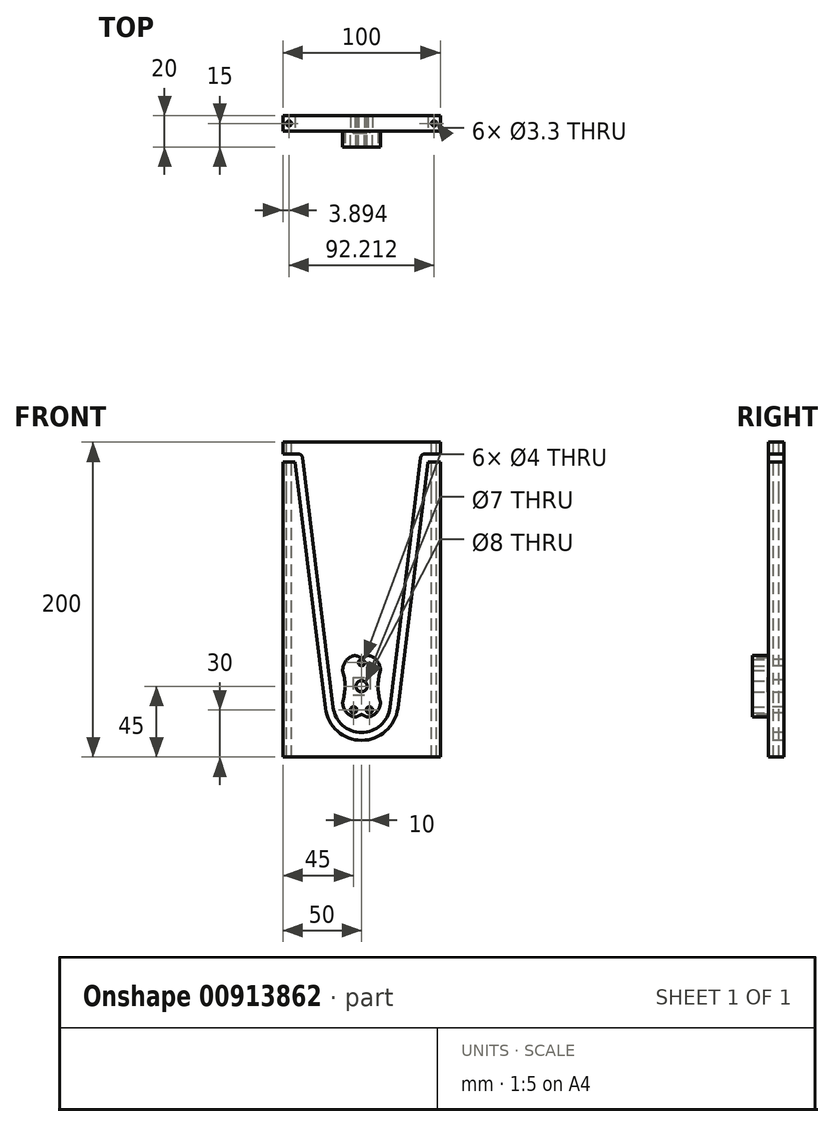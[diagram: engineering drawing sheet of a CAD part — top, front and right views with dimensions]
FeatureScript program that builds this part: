
annotation { "Feature Type Name" : "Feature", "Feature Type Description" : "" }
export const myFeature = defineFeature(function(context is Context, id is Id, definition is map)
    precondition{}
    {
        {
            var Q0;
            Q0=qCreatedBy(makeId("Front.planeOp"),FACE);
            var sketch = newSketch(context, id + "F0", { "sketchPlane" : qUnion([Q0])});
            skLineSegment(sketch, "E0.bottom", {"start": v(0, 0) * mm, "end": v(100, 0) * mm});
            skLineSegment(sketch, "E0.top", {"start": v(0, -200) * mm, "end": v(100, -200) * mm});
            skLineSegment(sketch, "E0.left", {"start": v(0, 0) * mm, "end": v(0, -200) * mm});
            skLineSegment(sketch, "E0.right", {"start": v(100, 0) * mm, "end": v(100, -200) * mm});
            skSolve(sketch);
        }
        {
            var Q0;
            Q0=makeQuery(id+"F0.imprint","IMPRINT",FACE,{"disambiguationData":[TD([[makeQuery(id+"F0.imprint","IMPRINT",EDGE,{"derivedFrom":sQuery(id+"F0.wireOp",EDGE,"E0.bottom")}),-1.0]])]});
            extrude(context, id + "F1", {"entities" : qUnion([Q0]), "depth" : 10 * mm, "offsetDistance" : 25 * mm});
        }
        {
            var Q0;
            Q0=makeQuery(id+"F1.opExtrude","CAP_FACE",FACE,{"disambiguationData":[OSD([sQuery(id+"F0.wireOp",EDGE,"E0.bottom"),sQuery(id+"F0.wireOp",EDGE,"E0.top"),sQuery(id+"F0.wireOp",EDGE,"E0.left"),sQuery(id+"F0.wireOp",EDGE,"E0.right")])],"isStart":false});
            var sketch = newSketch(context, id + "F2", { "sketchPlane" : qUnion([Q0])});
            skLineSegment(sketch, "E1", {"start": v(50, 0) * mm, "end": v(50, -200) * mm, "construction": true});
            skCircle(sketch, "E2", {"center": v(50, -155) * mm, "radius": 4 * mm});
            skCircle(sketch, "E3", {"center": v(55, -170) * mm, "radius": 2 * mm});
            skCircle(sketch, "E4", {"center": v(45, -170) * mm, "radius": 2 * mm});
            skCircle(sketch, "E5", {"center": v(50, -140) * mm, "radius": 2 * mm});
            skSolve(sketch);
        }
        {
            var Q0;
            Q0=qSketchRegion(id+"F2",true);
            extrude(context, id + "F3", {"entities" : qUnion([Q0]), "operationType" : NewBodyOperationType.REMOVE, "endBound" : BoundingType.THROUGH_ALL, "oppositeDirection" : true, "depth" : 25 * mm, "offsetDistance" : 25 * mm});
        }
        {
            var Q0;
            Q0=makeQuery(id+"F1.opExtrude","CAP_FACE",FACE,{"disambiguationData":[OSD([sQuery(id+"F0.wireOp",EDGE,"E0.bottom"),sQuery(id+"F0.wireOp",EDGE,"E0.top"),sQuery(id+"F0.wireOp",EDGE,"E0.left"),sQuery(id+"F0.wireOp",EDGE,"E0.right")])],"isStart":false});
            var sketch = newSketch(context, id + "F4", { "sketchPlane" : qUnion([Q0])});
            skLineSegment(sketch, "E6", {"start": v(50, 0) * mm, "end": v(50, -200) * mm, "construction": true});
            skLineSegment(sketch, "E7", {"start": v(0, -10) * mm, "end": v(10, -10) * mm});
            skLineSegment(sketch, "E8", {"start": v(10, -10) * mm, "end": v(29.48, -168.69) * mm});
            skArc(sketch, "E9", {"start": v(29.48, -168.69) * mm, "mid": v(36.3, -181.65) * mm, "end": v(50, -186.84) * mm});
            skLineSegment(sketch, "E10.MirrorCS", {"start": v(100, -10) * mm, "end": v(90, -10) * mm});
            skLineSegment(sketch, "E11.MirrorCS", {"start": v(90, -10) * mm, "end": v(70.52, -168.69) * mm});
            skArc(sketch, "E12.MirrorCS", {"start": v(70.52, -168.69) * mm, "mid": v(63.7, -181.65) * mm, "end": v(50, -186.84) * mm});
            skArc(sketch, "E13.0.startCap", {"start": v(87.52, -9.7) * mm, "mid": v(90.3, -7.52) * mm, "end": v(92.48, -10.3) * mm});
            skArc(sketch, "E13.0.endCap", {"start": v(73, -169) * mm, "mid": v(70.21, -171.17) * mm, "end": v(68.03, -168.38) * mm});
            skLineSegment(sketch, "E13.0.left", {"start": v(92.48, -10.3) * mm, "end": v(73, -169) * mm});
            skLineSegment(sketch, "E13.0.right", {"start": v(87.52, -9.7) * mm, "end": v(68.03, -168.38) * mm});
            skArc(sketch, "E13.1.startCap", {"start": v(100, -7.5) * mm, "mid": v(102.5, -10) * mm, "end": v(100, -12.5) * mm});
            skArc(sketch, "E13.1.endCap", {"start": v(90, -12.5) * mm, "mid": v(87.5, -10) * mm, "end": v(90, -7.5) * mm});
            skLineSegment(sketch, "E13.1.left", {"start": v(100, -12.5) * mm, "end": v(90, -12.5) * mm});
            skLineSegment(sketch, "E13.1.right", {"start": v(100, -7.5) * mm, "end": v(90, -7.5) * mm});
            skArc(sketch, "E13.2.startCap", {"start": v(0, -12.5) * mm, "mid": v(-2.5, -10) * mm, "end": v(0, -7.5) * mm});
            skArc(sketch, "E13.2.endCap", {"start": v(10, -7.5) * mm, "mid": v(12.5, -10) * mm, "end": v(10, -12.5) * mm});
            skLineSegment(sketch, "E13.2.left", {"start": v(0, -7.5) * mm, "end": v(10, -7.5) * mm});
            skLineSegment(sketch, "E13.2.right", {"start": v(0, -12.5) * mm, "end": v(10, -12.5) * mm});
            skArc(sketch, "E13.3.startCap", {"start": v(7.52, -10.3) * mm, "mid": v(9.7, -7.52) * mm, "end": v(12.48, -9.7) * mm});
            skArc(sketch, "E13.3.endCap", {"start": v(31.97, -168.38) * mm, "mid": v(29.79, -171.17) * mm, "end": v(27, -169) * mm});
            skLineSegment(sketch, "E13.3.left", {"start": v(12.48, -9.7) * mm, "end": v(31.97, -168.38) * mm});
            skLineSegment(sketch, "E13.3.right", {"start": v(7.52, -10.3) * mm, "end": v(27, -169) * mm});
            skArc(sketch, "E13.4.startCap", {"start": v(27, -169) * mm, "mid": v(29.18, -166.2) * mm, "end": v(31.97, -168.38) * mm});
            skArc(sketch, "E13.4.endCap", {"start": v(50, -184.34) * mm, "mid": v(52.5, -186.84) * mm, "end": v(50, -189.34) * mm});
            skArc(sketch, "E13.4.left", {"start": v(31.97, -168.38) * mm, "mid": v(37.96, -179.78) * mm, "end": v(50, -184.34) * mm});
            skArc(sketch, "E13.4.right", {"start": v(27, -169) * mm, "mid": v(34.65, -183.52) * mm, "end": v(50, -189.34) * mm});
            skArc(sketch, "E13.5.startCap", {"start": v(68.03, -168.38) * mm, "mid": v(70.82, -166.2) * mm, "end": v(73, -169) * mm});
            skArc(sketch, "E13.5.endCap", {"start": v(50, -189.34) * mm, "mid": v(47.5, -186.84) * mm, "end": v(50, -184.34) * mm});
            skArc(sketch, "E13.5.left", {"start": v(73, -169) * mm, "mid": v(65.35, -183.52) * mm, "end": v(50, -189.34) * mm});
            skArc(sketch, "E13.5.right", {"start": v(68.03, -168.38) * mm, "mid": v(62.04, -179.78) * mm, "end": v(50, -184.34) * mm});
            skSolve(sketch);
        }
        {
            var Q0;
            Q0=qSketchRegion(id+"F4",true);
            extrude(context, id + "F5", {"entities" : qUnion([Q0]), "operationType" : NewBodyOperationType.REMOVE, "endBound" : BoundingType.THROUGH_ALL, "oppositeDirection" : true, "depth" : 25 * mm, "offsetDistance" : 25 * mm});
        }
        {
            var Q0;
            Q0=makeQuery(id+"F1.opExtrude","SWEPT_FACE",FACE,{"disambiguationData":[OSD([sQuery(id+"F0.wireOp",EDGE,"E0.bottom")])]});
            var sketch = newSketch(context, id + "F6", { "sketchPlane" : qUnion([Q0])});
            skLineSegment(sketch, "E14", {"start": v(0, -10) * mm, "end": v(7.8, -10) * mm, "construction": true});
            skLineSegment(sketch, "E15", {"start": v(7.79, -10) * mm, "end": v(0, 0) * mm, "construction": true});
            skCircle(sketch, "E16", {"center": v(3.9, -5) * mm, "radius": 1.65 * mm});
            skLineSegment(sketch, "E17", {"start": v(100, -10) * mm, "end": v(92.2, -10) * mm, "construction": true});
            skLineSegment(sketch, "E18", {"start": v(92.2, -10) * mm, "end": v(100, 0) * mm, "construction": true});
            skCircle(sketch, "E19", {"center": v(96.1, -5) * mm, "radius": 1.65 * mm});
            skSolve(sketch);
        }
        {
            var Q0;
            Q0=makeQuery(id+"F5.boolean.opBoolean","COPY",FACE,{"derivedFrom":makeQuery(id+"F5.opExtrude","SWEPT_FACE",FACE,{"disambiguationData":[OSD([sQuery(id+"F4.wireOp",EDGE,"E13.1.left")])]})});
            var sketch = newSketch(context, id + "F7", { "sketchPlane" : qUnion([Q0])});
            skLineSegment(sketch, "E20", {"start": v(7.79, -10) * mm, "end": v(0, 0) * mm, "construction": true});
            skLineSegment(sketch, "E21", {"start": v(100, -10) * mm, "end": v(92.21, 0) * mm, "construction": true});
            skCircle(sketch, "E22", {"center": v(3.9, -5) * mm, "radius": 1.65 * mm});
            skCircle(sketch, "E23", {"center": v(96.1, -5) * mm, "radius": 1.65 * mm});
            skSolve(sketch);
        }
        {
            var Q0;
            Q0=qSketchRegion(id+"F7",true);
            extrude(context, id + "F8", {"entities" : qUnion([Q0]), "operationType" : NewBodyOperationType.REMOVE, "oppositeDirection" : true, "depth" : 20 * mm, "offsetDistance" : 25 * mm});
        }
        {
            var Q0;
            Q0=qSketchRegion(id+"F6",true);
            extrude(context, id + "F9", {"entities" : qUnion([Q0]), "operationType" : NewBodyOperationType.REMOVE, "endBound" : BoundingType.THROUGH_ALL, "oppositeDirection" : true, "depth" : 25 * mm, "offsetDistance" : 25 * mm});
        }
        {
            var Q0;
            {var subQ0=sQuery(id+"F0.wireOp",EDGE,"E0.bottom");var subQ1=sQuery(id+"F0.wireOp",EDGE,"E0.left");var subQ2=sQuery(id+"F0.wireOp",EDGE,"E0.right");Q0=makeQuery(id+"F5.boolean.opBoolean","SPLIT",FACE,{"disambiguationData":[TD([makeQuery(id+"F1.opExtrude","SWEPT_FACE",FACE,{"disambiguationData":[OSD([subQ0])]})])],"derivedFrom":makeQuery(id+"F1.opExtrude","CAP_FACE",FACE,{"disambiguationData":[OSD([subQ0,sQuery(id+"F0.wireOp",EDGE,"E0.top"),subQ1,subQ2])],"isStart":false})});}
            var sketch = newSketch(context, id + "F10", { "sketchPlane" : qUnion([Q0])});
            skCircle(sketch, "E24", {"center": v(50, -140) * mm, "radius": 2 * mm});
            skCircle(sketch, "E25", {"center": v(45, -170) * mm, "radius": 2 * mm});
            skCircle(sketch, "E26", {"center": v(55, -170) * mm, "radius": 2 * mm});
            skCircle(sketch, "E27", {"center": v(50, -155) * mm, "radius": 3.5 * mm});
            skLineSegment(sketch, "E28.bottom", {"start": v(62, -135) * mm, "end": v(38, -135) * mm});
            skLineSegment(sketch, "E28.top", {"start": v(62, -175) * mm, "end": v(38, -175) * mm});
            skLineSegment(sketch, "E28.left", {"start": v(62, -135) * mm, "end": v(62, -175) * mm});
            skLineSegment(sketch, "E28.right", {"start": v(38, -135) * mm, "end": v(38, -175) * mm});
            skLineSegment(sketch, "E29.bottom", {"start": v(60, -145) * mm, "end": v(40, -145) * mm, "construction": true});
            skLineSegment(sketch, "E29.top", {"start": v(60, -165) * mm, "end": v(40, -165) * mm, "construction": true});
            skLineSegment(sketch, "E29.left", {"start": v(60, -145) * mm, "end": v(60, -165) * mm, "construction": true});
            skLineSegment(sketch, "E29.right", {"start": v(40, -145) * mm, "end": v(40, -165) * mm, "construction": true});
            skSolve(sketch);
        }
        {
            var Q0;
            Q0 = qSketchRegion(id + "F10", true);
            extrude(context, id + "F11", {"entities" : qUnion([Q0]), "depth" : 10 * mm, "offsetDistance" : 25 * mm});
        }
        {
            var Q0;
            Q0=makeQuery(id+"F11.opExtrude","SWEPT_EDGE",EDGE,{"disambiguationData":[OSD([sQuery(id+"F10.wireOp",EDGE,"E28.bottom"),sQuery(id+"F10.wireOp",EDGE,"E28.left")])]});
            var Q1;
            Q1=makeQuery(id+"F11.opExtrude","SWEPT_EDGE",EDGE,{"disambiguationData":[OSD([sQuery(id+"F10.wireOp",EDGE,"E28.bottom"),sQuery(id+"F10.wireOp",EDGE,"E28.right")])]});
            var Q2;
            Q2=makeQuery(id+"F11.opExtrude","SWEPT_EDGE",EDGE,{"disambiguationData":[OSD([sQuery(id+"F10.wireOp",EDGE,"E28.top"),sQuery(id+"F10.wireOp",EDGE,"E28.right")])]});
            var Q3;
            Q3=makeQuery(id+"F11.opExtrude","SWEPT_EDGE",EDGE,{"disambiguationData":[OSD([sQuery(id+"F10.wireOp",EDGE,"E28.top"),sQuery(id+"F10.wireOp",EDGE,"E28.left")])]});
            fillet(context, id + "F12", {"entities" : qUnion([Q0, Q1, Q2, Q3]), "tangentPropagation" : true, "radius" : 10 * mm, "defaultsChanged" : false, "vertexSettings" : [], "allowEdgeOverflow" : false});
        }
        {
            var Q0;
            Q0=makeQuery(id+"F11.opExtrude","CAP_FACE",FACE,{"disambiguationData":[OSD([sQuery(id+"F10.wireOp",EDGE,"E24"),sQuery(id+"F10.wireOp",EDGE,"E25"),sQuery(id+"F10.wireOp",EDGE,"E26"),sQuery(id+"F10.wireOp",EDGE,"E27"),sQuery(id+"F10.wireOp",EDGE,"E28.bottom"),sQuery(id+"F10.wireOp",EDGE,"E28.top"),sQuery(id+"F10.wireOp",EDGE,"E28.left"),sQuery(id+"F10.wireOp",EDGE,"E28.right")])],"isStart":false});
            var sketch = newSketch(context, id + "F13", { "sketchPlane" : qUnion([Q0])});
            skArc(sketch, "E30", {"start": v(38, -165) * mm, "mid": v(39.5, -155) * mm, "end": v(38, -145) * mm});
            skArc(sketch, "E31", {"start": v(48, -135) * mm, "mid": v(50, -137) * mm, "end": v(52, -135) * mm});
            skLineSegment(sketch, "E32", {"start": v(50, -155) * mm, "end": v(60.05, -155) * mm, "construction": true});
            skLineSegment(sketch, "E33", {"start": v(50, -155) * mm, "end": v(50, -144.83) * mm, "construction": true});
            skLineSegment(sketch, "E34", {"start": v(38, -165) * mm, "end": v(38, -145) * mm});
            skLineSegment(sketch, "E35", {"start": v(48, -135) * mm, "end": v(52, -135) * mm});
            skArc(sketch, "E36.MirrorCS", {"start": v(62, -165) * mm, "mid": v(60.5, -155) * mm, "end": v(62, -145) * mm});
            skLineSegment(sketch, "E37.MirrorCS", {"start": v(62, -165) * mm, "end": v(62, -145) * mm});
            skArc(sketch, "E38.MirrorCS", {"start": v(48, -175) * mm, "mid": v(50, -173) * mm, "end": v(52, -175) * mm});
            skLineSegment(sketch, "E39.MirrorCS", {"start": v(48, -175) * mm, "end": v(52, -175) * mm});
            skSolve(sketch);
        }
        {
            var Q0;
            Q0 = qSketchRegion(id + "F13", true);
            extrude(context, id + "F14", {"entities" : qUnion([Q0]), "operationType" : NewBodyOperationType.REMOVE, "endBound" : BoundingType.UP_TO_NEXT, "oppositeDirection" : true, "depth" : 25 * mm, "offsetDistance" : 25 * mm});
        }
        {
            var Q0;
            {var subQ0=sQuery(id+"F10.wireOp",EDGE,"E28.right");var subQ1=makeQuery(id+"F11.opExtrude","SWEPT_FACE",FACE,{"disambiguationData":[OSD([subQ0])]});var subQ2=sQuery(id+"F10.wireOp",EDGE,"E28.left");var subQ3=sQuery(id+"F10.wireOp",EDGE,"E28.top");var subQ4=sQuery(id+"F10.wireOp",EDGE,"E28.bottom");var subQ5=sQuery(id+"F10.wireOp",EDGE,"E27");var subQ6=sQuery(id+"F10.wireOp",EDGE,"E26");var subQ7=sQuery(id+"F10.wireOp",EDGE,"E25");var subQ8=sQuery(id+"F10.wireOp",EDGE,"E24");var subQ9=makeQuery(id+"F11.opExtrude","SWEPT_EDGE",EDGE,{"disambiguationData":[OSD([subQ3,subQ0])]});Q0=makeQuery(id+"F14.boolean.opBoolean","MERGE",EDGE,{"derivedFrom":[makeQuery(id+"F12.opFillet","BLEND_EDGE",EDGE,{"blendedFrom":[subQ9,subQ1],"blendedInto":[subQ1]})],"fromTools":[makeQuery(id+"F14.opExtrude","SWEPT_EDGE",EDGE,{"disambiguationData":[OSD([subQ8,subQ7,subQ6,subQ5,subQ4,subQ3,subQ2,subQ0]),TDD([makeQuery(id+"F12.opFillet","BLEND_VERTEX",VERTEX,{"blendedFrom":[subQ9,makeQuery(id+"F11.opExtrude","CAP_FACE",FACE,{"disambiguationData":[OSD([subQ8,subQ7,subQ6,subQ5,subQ4,subQ3,subQ2,subQ0])],"isStart":true}),subQ1],"blendedInto":[makeQuery(id+"F11.opExtrude","CAP_FACE",FACE,{"disambiguationData":[OSD([subQ8,subQ7,subQ6,subQ5,subQ4,subQ3,subQ2,subQ0])],"isStart":true}),subQ1]})])]})]});}
            var Q1;
            {var subQ0=sQuery(id+"F10.wireOp",EDGE,"E28.left");var subQ1=makeQuery(id+"F11.opExtrude","SWEPT_FACE",FACE,{"disambiguationData":[OSD([subQ0])]});var subQ2=sQuery(id+"F10.wireOp",EDGE,"E28.right");var subQ3=sQuery(id+"F10.wireOp",EDGE,"E28.top");var subQ4=sQuery(id+"F10.wireOp",EDGE,"E28.bottom");var subQ5=sQuery(id+"F10.wireOp",EDGE,"E27");var subQ6=sQuery(id+"F10.wireOp",EDGE,"E26");var subQ7=sQuery(id+"F10.wireOp",EDGE,"E25");var subQ8=sQuery(id+"F10.wireOp",EDGE,"E24");var subQ9=makeQuery(id+"F11.opExtrude","SWEPT_EDGE",EDGE,{"disambiguationData":[OSD([subQ4,subQ0])]});Q1=makeQuery(id+"F14.boolean.opBoolean","MERGE",EDGE,{"derivedFrom":[makeQuery(id+"F12.opFillet","BLEND_EDGE",EDGE,{"blendedFrom":[subQ9,subQ1],"blendedInto":[subQ1]})],"fromTools":[makeQuery(id+"F14.opExtrude","SWEPT_EDGE",EDGE,{"disambiguationData":[OSD([subQ8,subQ7,subQ6,subQ5,subQ4,subQ3,subQ0,subQ2]),TDD([makeQuery(id+"F12.opFillet","BLEND_VERTEX",VERTEX,{"blendedFrom":[subQ9,makeQuery(id+"F11.opExtrude","CAP_FACE",FACE,{"disambiguationData":[OSD([subQ8,subQ7,subQ6,subQ5,subQ4,subQ3,subQ0,subQ2])],"isStart":true}),subQ1],"blendedInto":[makeQuery(id+"F11.opExtrude","CAP_FACE",FACE,{"disambiguationData":[OSD([subQ8,subQ7,subQ6,subQ5,subQ4,subQ3,subQ0,subQ2])],"isStart":true}),subQ1]})])]})]});}
            var Q2;
            {var subQ0=sQuery(id+"F10.wireOp",EDGE,"E28.left");var subQ1=makeQuery(id+"F11.opExtrude","SWEPT_FACE",FACE,{"disambiguationData":[OSD([subQ0])]});var subQ2=sQuery(id+"F10.wireOp",EDGE,"E28.right");var subQ3=sQuery(id+"F10.wireOp",EDGE,"E28.top");var subQ4=sQuery(id+"F10.wireOp",EDGE,"E28.bottom");var subQ5=sQuery(id+"F10.wireOp",EDGE,"E27");var subQ6=sQuery(id+"F10.wireOp",EDGE,"E26");var subQ7=sQuery(id+"F10.wireOp",EDGE,"E25");var subQ8=sQuery(id+"F10.wireOp",EDGE,"E24");var subQ9=makeQuery(id+"F11.opExtrude","SWEPT_EDGE",EDGE,{"disambiguationData":[OSD([subQ3,subQ0])]});Q2=makeQuery(id+"F14.boolean.opBoolean","MERGE",EDGE,{"derivedFrom":[makeQuery(id+"F12.opFillet","BLEND_EDGE",EDGE,{"blendedFrom":[subQ9,subQ1],"blendedInto":[subQ1]})],"fromTools":[makeQuery(id+"F14.opExtrude","SWEPT_EDGE",EDGE,{"disambiguationData":[OSD([subQ8,subQ7,subQ6,subQ5,subQ4,subQ3,subQ0,subQ2]),TDD([makeQuery(id+"F12.opFillet","BLEND_VERTEX",VERTEX,{"blendedFrom":[subQ9,makeQuery(id+"F11.opExtrude","CAP_FACE",FACE,{"disambiguationData":[OSD([subQ8,subQ7,subQ6,subQ5,subQ4,subQ3,subQ0,subQ2])],"isStart":true}),subQ1],"blendedInto":[makeQuery(id+"F11.opExtrude","CAP_FACE",FACE,{"disambiguationData":[OSD([subQ8,subQ7,subQ6,subQ5,subQ4,subQ3,subQ0,subQ2])],"isStart":true}),subQ1]})])]})]});}
            var Q3;
            {var subQ0=sQuery(id+"F10.wireOp",EDGE,"E28.bottom");var subQ1=makeQuery(id+"F11.opExtrude","SWEPT_FACE",FACE,{"disambiguationData":[OSD([subQ0])]});var subQ2=sQuery(id+"F10.wireOp",EDGE,"E28.right");var subQ3=sQuery(id+"F10.wireOp",EDGE,"E28.left");var subQ4=sQuery(id+"F10.wireOp",EDGE,"E28.top");var subQ5=sQuery(id+"F10.wireOp",EDGE,"E27");var subQ6=sQuery(id+"F10.wireOp",EDGE,"E26");var subQ7=sQuery(id+"F10.wireOp",EDGE,"E25");var subQ8=sQuery(id+"F10.wireOp",EDGE,"E24");var subQ9=makeQuery(id+"F11.opExtrude","SWEPT_EDGE",EDGE,{"disambiguationData":[OSD([subQ0,subQ2])]});Q3=makeQuery(id+"F14.boolean.opBoolean","MERGE",EDGE,{"derivedFrom":[makeQuery(id+"F12.opFillet","BLEND_EDGE",EDGE,{"blendedFrom":[subQ9,subQ1],"blendedInto":[subQ1]})],"fromTools":[makeQuery(id+"F14.opExtrude","SWEPT_EDGE",EDGE,{"disambiguationData":[OSD([subQ8,subQ7,subQ6,subQ5,subQ0,subQ4,subQ3,subQ2]),TDD([makeQuery(id+"F12.opFillet","BLEND_VERTEX",VERTEX,{"blendedFrom":[subQ9,makeQuery(id+"F11.opExtrude","CAP_FACE",FACE,{"disambiguationData":[OSD([subQ8,subQ7,subQ6,subQ5,subQ0,subQ4,subQ3,subQ2])],"isStart":true}),subQ1],"blendedInto":[makeQuery(id+"F11.opExtrude","CAP_FACE",FACE,{"disambiguationData":[OSD([subQ8,subQ7,subQ6,subQ5,subQ0,subQ4,subQ3,subQ2])],"isStart":true}),subQ1]})])]})]});}
            var Q4;
            {var subQ0=sQuery(id+"F10.wireOp",EDGE,"E28.bottom");var subQ1=makeQuery(id+"F11.opExtrude","SWEPT_FACE",FACE,{"disambiguationData":[OSD([subQ0])]});var subQ2=sQuery(id+"F10.wireOp",EDGE,"E28.right");var subQ3=sQuery(id+"F10.wireOp",EDGE,"E28.left");var subQ4=sQuery(id+"F10.wireOp",EDGE,"E28.top");var subQ5=sQuery(id+"F10.wireOp",EDGE,"E27");var subQ6=sQuery(id+"F10.wireOp",EDGE,"E26");var subQ7=sQuery(id+"F10.wireOp",EDGE,"E25");var subQ8=sQuery(id+"F10.wireOp",EDGE,"E24");var subQ9=makeQuery(id+"F11.opExtrude","SWEPT_EDGE",EDGE,{"disambiguationData":[OSD([subQ0,subQ3])]});Q4=makeQuery(id+"F14.boolean.opBoolean","MERGE",EDGE,{"derivedFrom":[makeQuery(id+"F12.opFillet","BLEND_EDGE",EDGE,{"blendedFrom":[subQ9,subQ1],"blendedInto":[subQ1]})],"fromTools":[makeQuery(id+"F14.opExtrude","SWEPT_EDGE",EDGE,{"disambiguationData":[OSD([subQ8,subQ7,subQ6,subQ5,subQ0,subQ4,subQ3,subQ2]),TDD([makeQuery(id+"F12.opFillet","BLEND_VERTEX",VERTEX,{"blendedFrom":[subQ9,makeQuery(id+"F11.opExtrude","CAP_FACE",FACE,{"disambiguationData":[OSD([subQ8,subQ7,subQ6,subQ5,subQ0,subQ4,subQ3,subQ2])],"isStart":true}),subQ1],"blendedInto":[makeQuery(id+"F11.opExtrude","CAP_FACE",FACE,{"disambiguationData":[OSD([subQ8,subQ7,subQ6,subQ5,subQ0,subQ4,subQ3,subQ2])],"isStart":true}),subQ1]})])]})]});}
            var Q5;
            {var subQ0=sQuery(id+"F10.wireOp",EDGE,"E28.top");var subQ1=makeQuery(id+"F11.opExtrude","SWEPT_FACE",FACE,{"disambiguationData":[OSD([subQ0])]});var subQ2=sQuery(id+"F10.wireOp",EDGE,"E28.right");var subQ3=sQuery(id+"F10.wireOp",EDGE,"E28.left");var subQ4=sQuery(id+"F10.wireOp",EDGE,"E28.bottom");var subQ5=sQuery(id+"F10.wireOp",EDGE,"E27");var subQ6=sQuery(id+"F10.wireOp",EDGE,"E26");var subQ7=sQuery(id+"F10.wireOp",EDGE,"E25");var subQ8=sQuery(id+"F10.wireOp",EDGE,"E24");var subQ9=makeQuery(id+"F11.opExtrude","SWEPT_EDGE",EDGE,{"disambiguationData":[OSD([subQ0,subQ3])]});Q5=makeQuery(id+"F14.boolean.opBoolean","MERGE",EDGE,{"derivedFrom":[makeQuery(id+"F12.opFillet","BLEND_EDGE",EDGE,{"blendedFrom":[subQ9,subQ1],"blendedInto":[subQ1]})],"fromTools":[makeQuery(id+"F14.opExtrude","SWEPT_EDGE",EDGE,{"disambiguationData":[OSD([subQ8,subQ7,subQ6,subQ5,subQ4,subQ0,subQ3,subQ2]),TDD([makeQuery(id+"F12.opFillet","BLEND_VERTEX",VERTEX,{"blendedFrom":[subQ9,makeQuery(id+"F11.opExtrude","CAP_FACE",FACE,{"disambiguationData":[OSD([subQ8,subQ7,subQ6,subQ5,subQ4,subQ0,subQ3,subQ2])],"isStart":true}),subQ1],"blendedInto":[makeQuery(id+"F11.opExtrude","CAP_FACE",FACE,{"disambiguationData":[OSD([subQ8,subQ7,subQ6,subQ5,subQ4,subQ0,subQ3,subQ2])],"isStart":true}),subQ1]})])]})]});}
            var Q6;
            {var subQ0=sQuery(id+"F10.wireOp",EDGE,"E28.top");var subQ1=makeQuery(id+"F11.opExtrude","SWEPT_FACE",FACE,{"disambiguationData":[OSD([subQ0])]});var subQ2=sQuery(id+"F10.wireOp",EDGE,"E28.right");var subQ3=sQuery(id+"F10.wireOp",EDGE,"E28.left");var subQ4=sQuery(id+"F10.wireOp",EDGE,"E28.bottom");var subQ5=sQuery(id+"F10.wireOp",EDGE,"E27");var subQ6=sQuery(id+"F10.wireOp",EDGE,"E26");var subQ7=sQuery(id+"F10.wireOp",EDGE,"E25");var subQ8=sQuery(id+"F10.wireOp",EDGE,"E24");var subQ9=makeQuery(id+"F11.opExtrude","SWEPT_EDGE",EDGE,{"disambiguationData":[OSD([subQ0,subQ2])]});Q6=makeQuery(id+"F14.boolean.opBoolean","MERGE",EDGE,{"derivedFrom":[makeQuery(id+"F12.opFillet","BLEND_EDGE",EDGE,{"blendedFrom":[subQ9,subQ1],"blendedInto":[subQ1]})],"fromTools":[makeQuery(id+"F14.opExtrude","SWEPT_EDGE",EDGE,{"disambiguationData":[OSD([subQ8,subQ7,subQ6,subQ5,subQ4,subQ0,subQ3,subQ2]),TDD([makeQuery(id+"F12.opFillet","BLEND_VERTEX",VERTEX,{"blendedFrom":[subQ9,makeQuery(id+"F11.opExtrude","CAP_FACE",FACE,{"disambiguationData":[OSD([subQ8,subQ7,subQ6,subQ5,subQ4,subQ0,subQ3,subQ2])],"isStart":true}),subQ1],"blendedInto":[makeQuery(id+"F11.opExtrude","CAP_FACE",FACE,{"disambiguationData":[OSD([subQ8,subQ7,subQ6,subQ5,subQ4,subQ0,subQ3,subQ2])],"isStart":true}),subQ1]})])]})]});}
            fillet(context, id + "F15", {"entities" : qUnion([Q0, Q1, Q2, Q3, Q4, Q5, Q6]), "tangentPropagation" : true, "radius" : 5 * mm, "defaultsChanged" : false, "vertexSettings" : [], "allowEdgeOverflow" : false});
        }
        {
            var Q0;
            Q0=makeQuery(id+"F11.opExtrude","CAP_FACE",FACE,{"disambiguationData":[OSD([sQuery(id+"F10.wireOp",EDGE,"E24"),sQuery(id+"F10.wireOp",EDGE,"E25"),sQuery(id+"F10.wireOp",EDGE,"E26"),sQuery(id+"F10.wireOp",EDGE,"E27"),sQuery(id+"F10.wireOp",EDGE,"E28.bottom"),sQuery(id+"F10.wireOp",EDGE,"E28.top"),sQuery(id+"F10.wireOp",EDGE,"E28.left"),sQuery(id+"F10.wireOp",EDGE,"E28.right")])],"isStart":true});
            var sketch = newSketch(context, id + "F16", { "sketchPlane" : qUnion([Q0])});
            skLineSegment(sketch, "E40.bottom", {"start": v(-44.5, -149.5) * mm, "end": v(-55.5, -149.5) * mm});
            skLineSegment(sketch, "E40.top", {"start": v(-44.5, -160.5) * mm, "end": v(-55.5, -160.5) * mm});
            skLineSegment(sketch, "E40.left", {"start": v(-44.5, -149.5) * mm, "end": v(-44.5, -160.5) * mm});
            skLineSegment(sketch, "E40.right", {"start": v(-55.5, -149.5) * mm, "end": v(-55.5, -160.5) * mm});
            skPoint(sketch, "E40.middle", {"position": v(-50, -155) * mm});
            skSolve(sketch);
        }
        {
            var Q0;
            Q0 = qSketchRegion(id + "F16", true);
            extrude(context, id + "F17", {"entities" : qUnion([Q0]), "operationType" : NewBodyOperationType.REMOVE, "oppositeDirection" : true, "depth" : 1 * mm, "offsetDistance" : 25 * mm});
        }
    });
